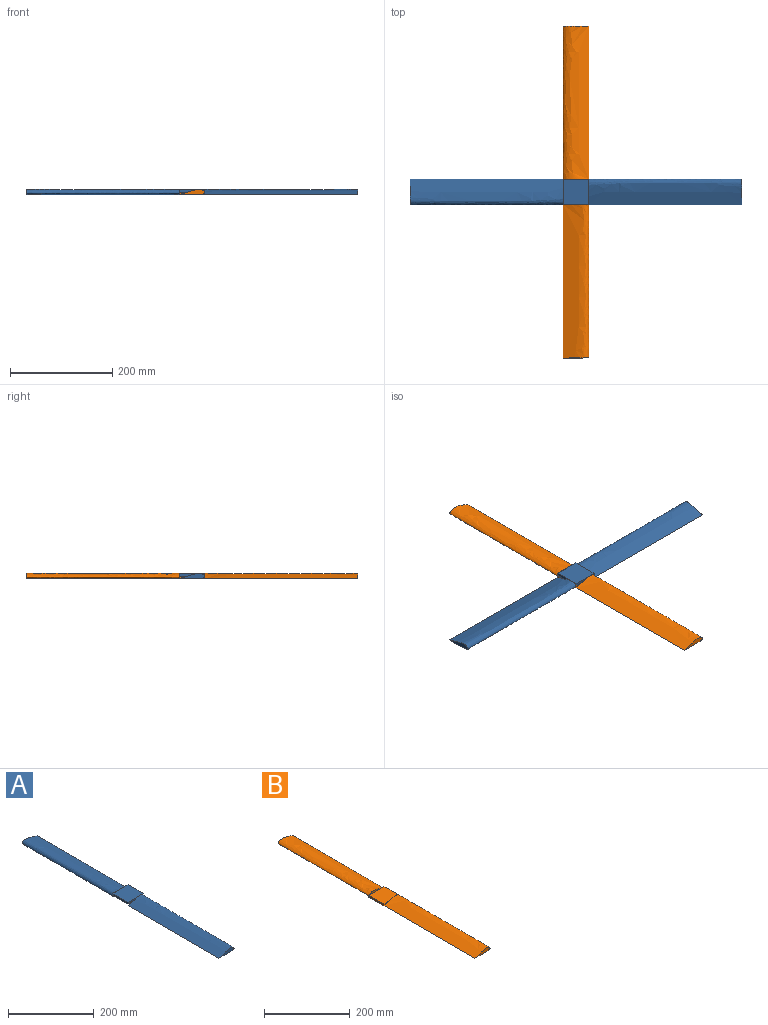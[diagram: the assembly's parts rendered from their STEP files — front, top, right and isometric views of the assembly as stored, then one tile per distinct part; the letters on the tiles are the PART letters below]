
ASSEMBLY  parts=2 mates=1
PART A: 18 faces, bbox 51.4x650x10.9 mm
  f0: plane 50x50mm, normal (0,0,1), area 2500mm2, adj f1,f2,f11,f12,f13,f15,f16,f17
  f1: plane 50x5mm, normal (-1,0,0), area 250mm2, adj f0,f9,f12,f17
  f2: plane 50x5mm, normal (1,0,0), area 250mm2, adj f0,f9,f13,f16
  f3: plane 50.72x10.87mm, normal (0,-1,0), area 312.2mm2, adj f5,f10
  f4: plane 50.15x5.14mm, normal (0,1,0), area 202.5mm2, adj f5,f9,f10
  f5: plane 300x37.5mm, normal (0,0,-1), area 11250mm2, adj f3,f4,f10
  f6: plane 50.72x10.87mm, normal (0,1,0), area 312.2mm2, adj f7,f14
  f7: plane 300x37.5mm, normal (0,0,-1), area 11250mm2, adj f6,f8,f14
  f8: plane 50.15x5.14mm, normal (0,-1,0), area 202.5mm2, adj f7,f9,f14
  f9: plane 50x50mm, normal (0,0,-1), area 2500mm2, adj f1,f2,f4,f8,f12,f13,f16,f17
  f10: extruded ~300x50.01mm, area 20505.6mm2, adj f3,f4,f5,f11,f12,f13
  f11: plane 5.42x0.28mm, normal (0,1,0), area 0.6mm2, adj f0,f10
  f12: plane 37.79x5.59mm, normal (0,-1,0), area 128.2mm2, adj f0,f1,f9,f10
  f13: plane 7.23x5.12mm, normal (0,-1,0), area 12.8mm2, adj f0,f2,f9,f10
  f14: extruded ~300x50.01mm, area 20505.6mm2, adj f6,f7,f8,f15,f16,f17
  f15: plane 5.42x0.28mm, normal (0,-1,0), area 0.6mm2, adj f0,f14
  f16: plane 37.79x5.59mm, normal (0,1,0), area 128.2mm2, adj f0,f2,f9,f14
  f17: plane 7.23x5.12mm, normal (0,1,0), area 12.8mm2, adj f0,f1,f9,f14
PART B: 18 faces, bbox 51.5x650x11 mm
  f0: plane 50.79x10.99mm, normal (0,1,0), area 339.3mm2, adj f5,f13
  f1: plane 38.29x6.08mm, normal (0,-1,0), area 130.3mm2, adj f7,f13
  f2: plane 50x5mm, normal (1,0,0), area 250mm2, adj f5,f7,f9,f11,f12,f16
  f3: plane 50x5mm, normal (-1,0,0), area 250mm2, adj f5,f7,f10,f14,f15,f17
  f4: plane 50.72x10.87mm, normal (0,-1,0), area 312.2mm2, adj f5,f8
  f5: plane 650x50mm, normal (0,0,-1), area 25000mm2, adj f0,f2,f3,f4,f8,f12,f13,f17
  f6: plane 34x5.75mm, normal (0,1,0), area 109.6mm2, adj f7,f8
  f7: plane 50x50mm, normal (0,0,1), area 2500mm2, adj f1,f2,f3,f6,f10,f11,f15,f16
  f8: extruded ~300x50.01mm, area 20505.6mm2, adj f4,f5,f6,f9,f10,f11,f12
  f9: plane 0.55x0.02mm, normal (0,1,0), area 0mm2, adj f2,f8
  f10: plane 16.31x5.04mm, normal (0,-1,0), area 40.3mm2, adj f3,f7,f8
  f11: plane 1.14x0.34mm, normal (0,-1,0), area 0.1mm2, adj f2,f7,f8
  f12: plane 12.78x3.47mm, normal (0,-1,0), area 7.1mm2, adj f2,f5,f8
  f13: extruded ~300x49.99mm, area 20250.7mm2, adj f0,f1,f5,f14,f15,f16,f17
  f14: plane 0.33x0.02mm, normal (0,-1,0), area 0mm2, adj f3,f13
  f15: plane 1.39x0.79mm, normal (0,1,0), area 0.4mm2, adj f3,f7,f13
  f16: plane 11.81x5.02mm, normal (0,1,0), area 28.9mm2, adj f2,f7,f13
  f17: plane 13.74x3.95mm, normal (0,1,0), area 11.7mm2, adj f3,f5,f13
PLACE A rot(axis=(0,0,1),90deg) t=(22.26,-18.87,-12.4)mm
PLACE B t=(22.26,-18.87,-2.4)mm
MATE fastened A.f9 <-> B.f7  axis (0,0,-1) through (22.26,-18.87,-7.4)mm
